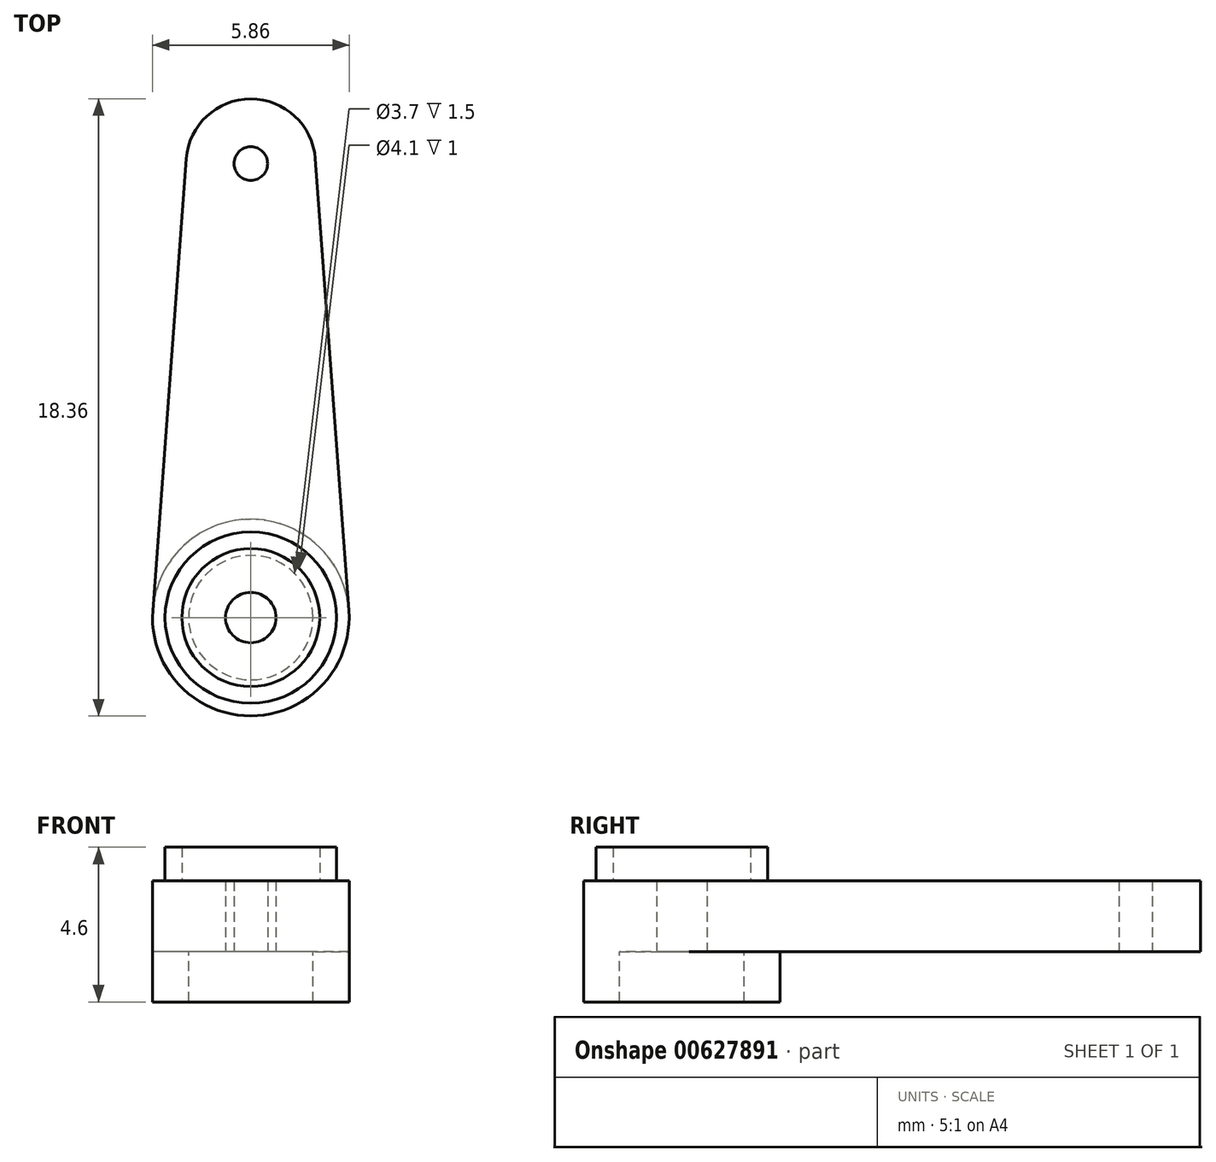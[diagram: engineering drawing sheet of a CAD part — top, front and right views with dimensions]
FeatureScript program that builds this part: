
annotation { "Feature Type Name" : "Feature", "Feature Type Description" : "" }
export const myFeature = defineFeature(function(context is Context, id is Id, definition is map)
    precondition{}
    {
        {
            var Q0;
            Q0=qCreatedBy(makeId("Top.planeOp"),FACE);
            var sketch = newSketch(context, id + "F0", { "sketchPlane" : qUnion([Q0])});
            skLineSegment(sketch, "E0", {"start": v(0, 0) * mm, "end": v(0, 24.29) * mm, "construction": true});
            skCircle(sketch, "E1", {"center": v(0, 0) * mm, "radius": 2.93 * mm});
            skCircle(sketch, "E2", {"center": v(0, 13.5) * mm, "radius": 1.93 * mm});
            skLineSegment(sketch, "E3", {"start": v(-1.92, 13.64) * mm, "end": v(-2.92, 0.22) * mm});
            skLineSegment(sketch, "E4", {"start": v(1.92, 13.64) * mm, "end": v(2.92, 0.22) * mm});
            skCircle(sketch, "E5", {"center": v(0, 0) * mm, "radius": 0.75 * mm});
            skCircle(sketch, "E6", {"center": v(0, 13.5) * mm, "radius": 0.5 * mm});
            skSolve(sketch);
        }
        {
            var Q0;
            Q0 = qSketchRegion(id + "F0", true);
            extrude(context, id + "F1", {"entities" : qUnion([Q0]), "depth" : 2.1 * mm, "offsetDistance" : 25 * mm});
        }
        {
            var Q0;
            {var subQ0=sQuery(id+"F0.wireOp",EDGE,"E1");var subQ1=makeQuery(id+"F0.imprint","INTERSECT",VERTEX,{"derivedFrom":[subQ0,sQuery(id+"F0.wireOp",EDGE,"E3")]});Q0=makeQuery(id+"F0.imprint","IMPRINT",FACE,{"disambiguationData":[TD([[makeQuery(id+"F0.imprint","IMPRINT",EDGE,{"disambiguationData":[TD([[subQ1,1.0]])],"derivedFrom":subQ0}),1.0]])]});}
            var sketch = newSketch(context, id + "F2", { "sketchPlane" : qUnion([Q0])});
            skArc(sketch, "E7.0.0", {"start": v(-2.92, 0.22) * mm, "mid": v(0, -2.93) * mm, "end": v(2.92, 0.22) * mm});
            skArc(sketch, "E7.0.1", {"start": v(2.92, 0.22) * mm, "mid": v(0, 2.93) * mm, "end": v(-2.92, 0.22) * mm});
            skCircle(sketch, "E8", {"center": v(0, 0) * mm, "radius": 1.85 * mm});
            skSolve(sketch);
        }
        {
            var Q0;
            Q0 = qSketchRegion(id + "F2", true);
            extrude(context, id + "F3", {"entities" : qUnion([Q0]), "operationType" : NewBodyOperationType.ADD, "oppositeDirection" : true, "depth" : 1.5 * mm, "offsetDistance" : 25 * mm});
        }
        {
            var Q0;
            Q0=makeQuery(id+"F1.opExtrude","CAP_FACE",FACE,{"disambiguationData":[OSD([sQuery(id+"F0.wireOp",EDGE,"E1"),sQuery(id+"F0.wireOp",EDGE,"E2"),sQuery(id+"F0.wireOp",EDGE,"E3"),sQuery(id+"F0.wireOp",EDGE,"E4"),sQuery(id+"F0.wireOp",EDGE,"E5"),sQuery(id+"F0.wireOp",EDGE,"E6")])],"isStart":false});
            var sketch = newSketch(context, id + "F4", { "sketchPlane" : qUnion([Q0])});
            skCircle(sketch, "E9.0", {"center": v(0, 0) * mm, "radius": 0.75 * mm, "construction": true});
            skCircle(sketch, "E10", {"center": v(0, 0) * mm, "radius": 2.55 * mm});
            skCircle(sketch, "E11", {"center": v(0, 0) * mm, "radius": 2.05 * mm});
            skSolve(sketch);
        }
        {
            var Q0;
            Q0 = qSketchRegion(id + "F4", true);
            extrude(context, id + "F5", {"entities" : qUnion([Q0]), "operationType" : NewBodyOperationType.ADD, "depth" : 1 * mm, "offsetDistance" : 25 * mm});
        }
    });
